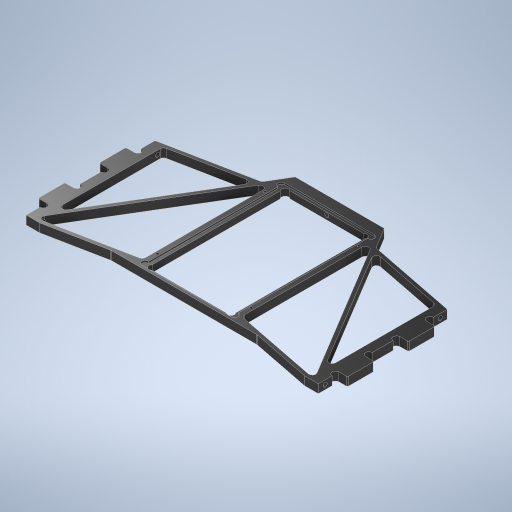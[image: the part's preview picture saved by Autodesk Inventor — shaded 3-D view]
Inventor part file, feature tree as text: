
AUTODESK INVENTOR PART (.ipt)
format: ipt  version: 2024.2 (Build 282272000, 272)  size: 603,648 bytes
history: native  units: mm
features: sketch x3, extrude x2, hole x2, chamfer x1, mirror x1
ambient origin geometry x8: Origin, YZ Plane, XZ Plane, XY Plane, X Axis, Y Axis, Z Axis, Center Point
bodies: Solid1 (feature_tree)
feature tree (9):
  sketch  "Sketch1"  dims[d1=170.0mm d2=2.0mm]
  extrude  "Extrusion1"  Depth=2.0mm
  extrude  "Extrusion2"  Depth=5.0mm TaperAngle=0.0deg
  hole  "SideーM3"  [1 undecoded]
  chamfer  "C0.5"  Distance=51.6mm
  mirror  "Mirror5"
  hole  "Back-M3"  [1 undecoded]
  sketch  "Sketch6"  dims[d3=5.0mm d12=5.0mm d13=0.0mm]
  sketch  "Sketch7"  dims[d37=0.5mm d38=2.0mm d39=45.0deg d55=82.6mm d56=51.6mm d57=0.25mm d58=0.25mm d59=2.0mm d61=2.0mm d62=2.0mm d63=2.0mm d68=1.0mm d69=0.0mm d81=3.0mm d82=2.0mm d85=1.5mm d86=1.5mm d87=1.567mm d88=4.0mm d89=4.0mm d90=2.0mm d91=90.0deg d92=8.0mm d93=20.594885mm d94=10.0mm d95=5.0mm d99=6.0mm d100=8.0mm d102=15.5mm d103=20.0mm d104=37.5mm d106=2.459mm d107=6.0mm d108=4.0mm d109=2.0mm d110=90.0deg d111=10.0mm d112=0.0mm d114=2.0mm d118=5.5mm d121=2.0mm d122=53.0mm d123=2.0mm d127=8.65mm d128=60.0mm d129=6.0mm d130=11.5mm d131=5.0mm d132=40.8mm d134=17.671459mm d139=1.5mm d141=2.0mm d143=2.0mm d144=2.459mm d145=6.0mm d146=4.0mm d147=2.0mm d148=90.0deg d149=8.0mm d150=20.594885mm]
note: 2 required parameter values undecoded (feature->parameter linkage not recoverable at this tier; creation-order binding heuristic only, values carry confidence <= 0.55)
